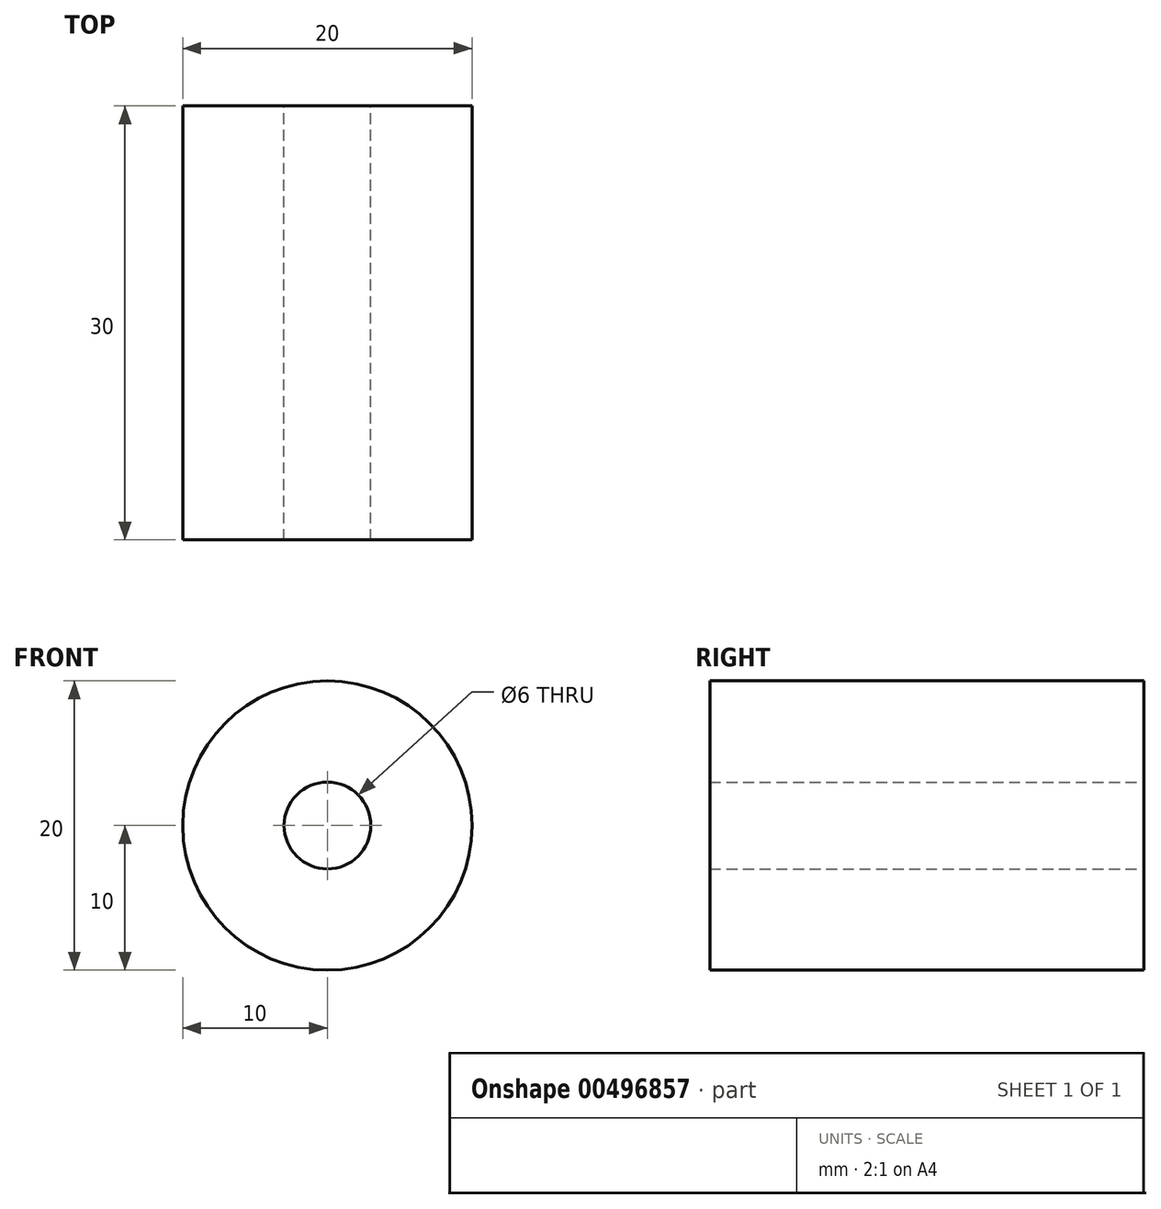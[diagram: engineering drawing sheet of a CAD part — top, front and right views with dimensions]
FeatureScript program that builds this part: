
annotation { "Feature Type Name" : "Feature", "Feature Type Description" : "" }
export const myFeature = defineFeature(function(context is Context, id is Id, definition is map)
    precondition{}
    {
        {
            var Q0;
            Q0=qCreatedBy(makeId("Front.planeOp"),FACE);
            var sketch = newSketch(context, id + "F0", { "sketchPlane" : qUnion([Q0])});
            skCircle(sketch, "E0", {"center": v(0, 0) * mm, "radius": 3 * mm});
            skCircle(sketch, "E1", {"center": v(0, 0) * mm, "radius": 10 * mm});
            skSolve(sketch);
        }
        {
            var Q0;
            Q0=makeQuery(id+"F0.imprint","IMPRINT",FACE,{"disambiguationData":[TD([[makeQuery(id+"F0.imprint","IMPRINT",EDGE,{"derivedFrom":sQuery(id+"F0.wireOp",EDGE,"E0")}),-1.0]])]});
            extrude(context, id + "F1", {"entities" : qUnion([Q0]), "depth" : 30 * mm, "offsetDistance" : 25 * mm});
        }
    });
